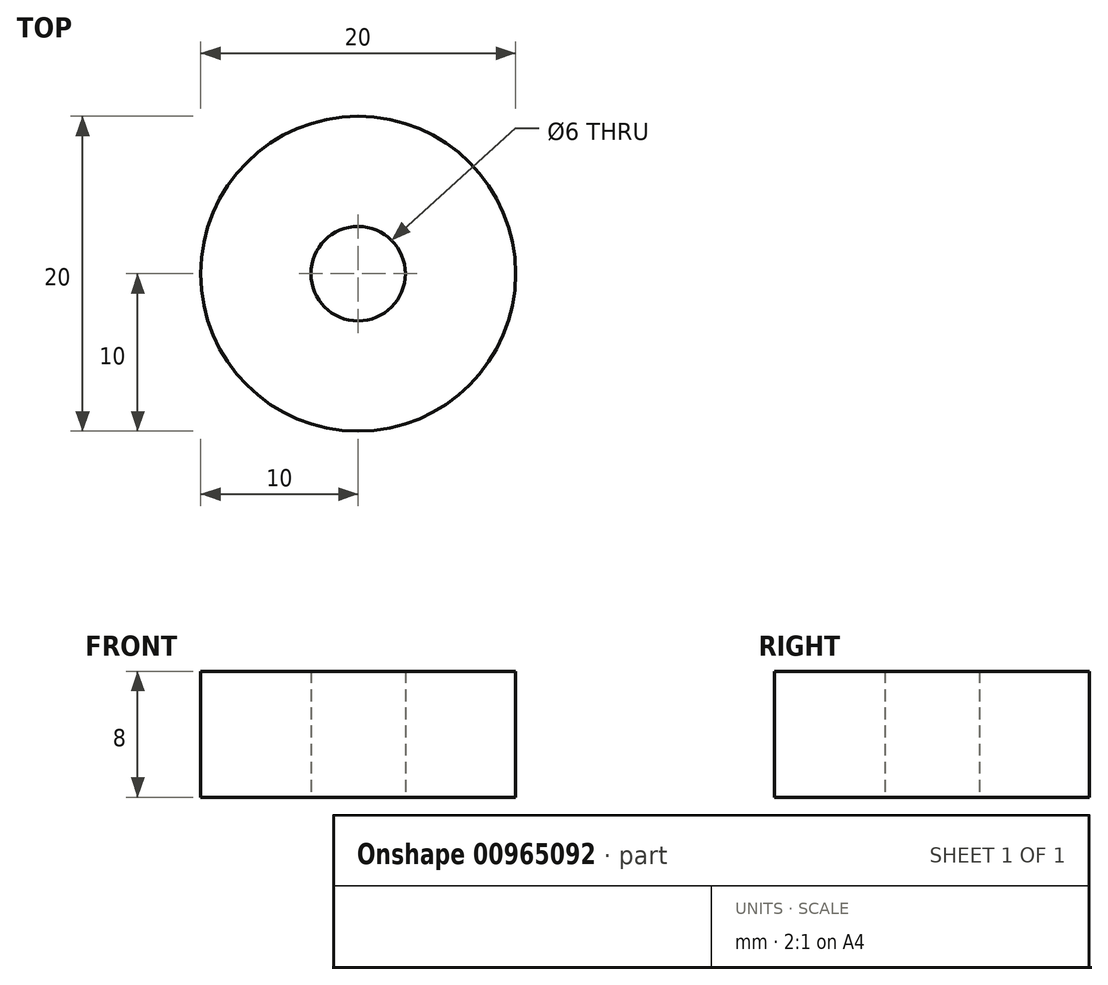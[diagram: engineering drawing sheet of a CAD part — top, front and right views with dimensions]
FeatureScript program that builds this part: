
annotation { "Feature Type Name" : "Feature", "Feature Type Description" : "" }
export const myFeature = defineFeature(function(context is Context, id is Id, definition is map)
    precondition{}
    {
        {
            var Q0;
            Q0=qCreatedBy(makeId("Top.planeOp"),FACE);
            var sketch = newSketch(context, id + "F0", { "sketchPlane" : qUnion([Q0])});
            skCircle(sketch, "E0", {"center": v(0, 0) * mm, "radius": 10 * mm});
            skCircle(sketch, "E1", {"center": v(0, 0) * mm, "radius": 3 * mm});
            skSolve(sketch);
        }
        {
            var Q0;
            Q0=makeQuery(id+"F0.imprint","IMPRINT",FACE,{"disambiguationData":[TD([[makeQuery(id+"F0.imprint","IMPRINT",EDGE,{"derivedFrom":sQuery(id+"F0.wireOp",EDGE,"E0")}),1.0]])]});
            extrude(context, id + "F1", {"entities" : qUnion([Q0]), "depth" : 8 * mm, "offsetDistance" : 25 * mm});
        }
    });
